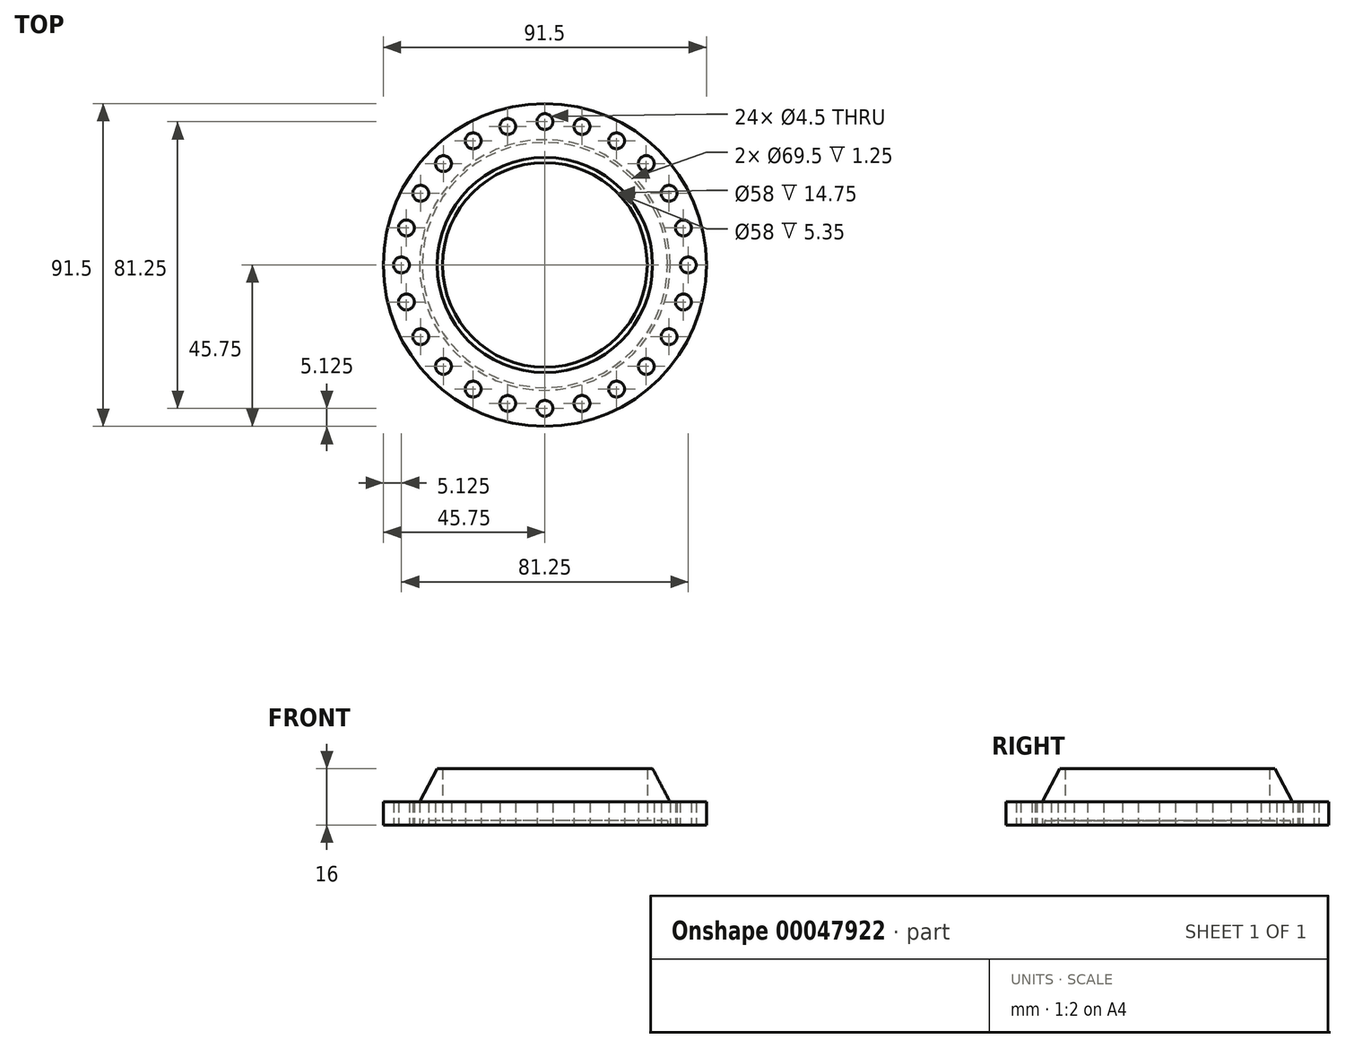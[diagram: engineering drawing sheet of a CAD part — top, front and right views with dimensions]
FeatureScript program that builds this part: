
annotation { "Feature Type Name" : "Feature", "Feature Type Description" : "" }
export const myFeature = defineFeature(function(context is Context, id is Id, definition is map)
    precondition{}
    {
        {
            var Q0;
            Q0=qCreatedBy(makeId("Top.planeOp"),FACE);
            var sketch = newSketch(context, id + "F0", { "sketchPlane" : qUnion([Q0])});
            skCircle(sketch, "E0", {"center": v(0, 0) * mm, "radius": 45.75 * mm});
            skCircle(sketch, "E1", {"center": v(0, 0) * mm, "radius": 40.62 * mm});
            skCircle(sketch, "E2", {"center": v(-40.62, 0) * mm, "radius": 2.25 * mm});
            skCircle(sketch, "E3", {"center": v(0, 0) * mm, "radius": 29 * mm});
            skCircle(sketch, "E4", {"center": v(0, 0) * mm, "radius": 35.5 * mm});
            skCircle(sketch, "E5.1.0", {"center": v(-39.24, -10.51) * mm, "radius": 2.25 * mm});
            skCircle(sketch, "E5.2.0", {"center": v(-35.18, -20.31) * mm, "radius": 2.25 * mm});
            skCircle(sketch, "E6.1.3.0", {"center": v(-28.73, -28.73) * mm, "radius": 2.25 * mm});
            skCircle(sketch, "E6.1.4.0", {"center": v(-20.31, -35.18) * mm, "radius": 2.25 * mm});
            skCircle(sketch, "E6.1.5.0", {"center": v(-10.51, -39.24) * mm, "radius": 2.25 * mm});
            skCircle(sketch, "E6.1.6.0", {"center": v(0, -40.62) * mm, "radius": 2.25 * mm});
            skCircle(sketch, "E6.1.7.0", {"center": v(10.51, -39.24) * mm, "radius": 2.25 * mm});
            skCircle(sketch, "E6.1.8.0", {"center": v(20.31, -35.18) * mm, "radius": 2.25 * mm});
            skCircle(sketch, "E6.1.9.0", {"center": v(28.73, -28.73) * mm, "radius": 2.25 * mm});
            skCircle(sketch, "E6.1.10.0", {"center": v(35.18, -20.31) * mm, "radius": 2.25 * mm});
            skCircle(sketch, "E6.1.11.0", {"center": v(39.24, -10.51) * mm, "radius": 2.25 * mm});
            skCircle(sketch, "E6.1.12.0", {"center": v(40.62, 0) * mm, "radius": 2.25 * mm});
            skCircle(sketch, "E6.1.13.0", {"center": v(39.24, 10.51) * mm, "radius": 2.25 * mm});
            skCircle(sketch, "E6.1.14.0", {"center": v(35.18, 20.31) * mm, "radius": 2.25 * mm});
            skCircle(sketch, "E6.1.15.0", {"center": v(28.73, 28.73) * mm, "radius": 2.25 * mm});
            skCircle(sketch, "E6.1.16.0", {"center": v(20.31, 35.18) * mm, "radius": 2.25 * mm});
            skCircle(sketch, "E6.1.17.0", {"center": v(10.51, 39.24) * mm, "radius": 2.25 * mm});
            skCircle(sketch, "E6.1.18.0", {"center": v(0, 40.62) * mm, "radius": 2.25 * mm});
            skCircle(sketch, "E6.1.19.0", {"center": v(-10.51, 39.24) * mm, "radius": 2.25 * mm});
            skCircle(sketch, "E6.1.20.0", {"center": v(-20.31, 35.18) * mm, "radius": 2.25 * mm});
            skCircle(sketch, "E6.1.21.0", {"center": v(-28.73, 28.73) * mm, "radius": 2.25 * mm});
            skCircle(sketch, "E6.1.22.0", {"center": v(-35.18, 20.31) * mm, "radius": 2.25 * mm});
            skCircle(sketch, "E7.1.23.0", {"center": v(-39.24, 10.51) * mm, "radius": 2.25 * mm});
            skSolve(sketch);
        }
        {
            var Q0;
            Q0=makeQuery(id+"F0.imprint","IMPRINT",FACE,{"disambiguationData":[TD([[makeQuery(id+"F0.imprint","IMPRINT",EDGE,{"derivedFrom":sQuery(id+"F0.wireOp",EDGE,"E0")}),1.0]])]});
            var Q1;
            Q1=makeQuery(id+"F0.imprint","IMPRINT",FACE,{"disambiguationData":[TD([[makeQuery(id+"F0.imprint","IMPRINT",EDGE,{"derivedFrom":sQuery(id+"F0.wireOp",EDGE,"E4")}),-1.0]])]});
            var Q2;
            Q2=makeQuery(id+"F0.imprint","IMPRINT",FACE,{"disambiguationData":[TD([[makeQuery(id+"F0.imprint","IMPRINT",EDGE,{"derivedFrom":sQuery(id+"F0.wireOp",EDGE,"E3")}),-1.0]])]});
            var Q3;
            Q3=sQuery(id+"F0.wireOp",EDGE,"E0");
            var Q4;
            Q4=sQuery(id+"F0.wireOp",EDGE,"E7.1.23.0");
            var Q5;
            Q5=sQuery(id+"F0.wireOp",EDGE,"E2");
            var Q6;
            Q6=sQuery(id+"F0.wireOp",EDGE,"E5.2.0");
            var Q7;
            Q7=sQuery(id+"F0.wireOp",EDGE,"E6.1.22.0");
            var Q8;
            Q8=sQuery(id+"F0.wireOp",EDGE,"E6.1.21.0");
            var Q9;
            Q9=sQuery(id+"F0.wireOp",EDGE,"E6.1.20.0");
            var Q10;
            Q10=sQuery(id+"F0.wireOp",EDGE,"E6.1.19.0");
            var Q11;
            Q11=sQuery(id+"F0.wireOp",EDGE,"E6.1.18.0");
            var Q12;
            Q12=sQuery(id+"F0.wireOp",EDGE,"E6.1.17.0");
            var Q13;
            Q13=sQuery(id+"F0.wireOp",EDGE,"E6.1.16.0");
            var Q14;
            Q14=sQuery(id+"F0.wireOp",EDGE,"E6.1.15.0");
            var Q15;
            Q15=sQuery(id+"F0.wireOp",EDGE,"E6.1.14.0");
            var Q16;
            Q16=sQuery(id+"F0.wireOp",EDGE,"E6.1.13.0");
            var Q17;
            Q17=sQuery(id+"F0.wireOp",EDGE,"E6.1.12.0");
            var Q18;
            Q18=sQuery(id+"F0.wireOp",EDGE,"E6.1.11.0");
            var Q19;
            Q19=sQuery(id+"F0.wireOp",EDGE,"E6.1.10.0");
            var Q20;
            Q20=sQuery(id+"F0.wireOp",EDGE,"E6.1.9.0");
            var Q21;
            Q21=sQuery(id+"F0.wireOp",EDGE,"E6.1.8.0");
            var Q22;
            Q22=sQuery(id+"F0.wireOp",EDGE,"E6.1.7.0");
            var Q23;
            Q23=sQuery(id+"F0.wireOp",EDGE,"E6.1.6.0");
            var Q24;
            Q24=sQuery(id+"F0.wireOp",EDGE,"E6.1.5.0");
            var Q25;
            Q25=sQuery(id+"F0.wireOp",EDGE,"E6.1.4.0");
            var Q26;
            Q26=sQuery(id+"F0.wireOp",EDGE,"E6.1.3.0");
            var Q27;
            Q27=sQuery(id+"F0.wireOp",EDGE,"E5.1.0");
            var Q28;
            Q28=sQuery(id+"F0.wireOp",EDGE,"E4");
            var Q29;
            Q29=qCreatedBy(makeId("Front.planeOp"),FACE);
            extrude(context, id + "F1", {"entities" : qUnion([Q0, Q1, Q2]), "surfaceEntities" : qUnion([Q3, Q4, Q5, Q6, Q7, Q8, Q9, Q10, Q11, Q12, Q13, Q14, Q15, Q16, Q17, Q18, Q19, Q20, Q21, Q22, Q23, Q24, Q25, Q26, Q27, Q28]), "endBoundEntityFace" : qUnion([Q29]), "depth" : 6.6 * mm});
        }
        {
            var Q0;
            Q0=sQuery(id+"F0.wireOp",EDGE,"E3");
            extrude(context, id + "F2", {"bodyType" : ToolBodyType.SURFACE, "surfaceEntities" : qUnion([Q0]), "depth" : 16 * mm});
        }
        {
            var Q0;
            Q0=makeQuery(id+"F0.imprint","IMPRINT",FACE,{"disambiguationData":[TD([[makeQuery(id+"F0.imprint","IMPRINT",EDGE,{"derivedFrom":sQuery(id+"F0.wireOp",EDGE,"E3")}),-1.0]])]});
            extrude(context, id + "F3", {"entities" : qUnion([Q0]), "depth" : 16 * mm});
        }
        {
            var Q0;
            Q0=makeQuery(id+"F3.opExtrude","CAP_EDGE",EDGE,{"disambiguationData":[OSD([sQuery(id+"F0.wireOp",EDGE,"E4")])],"isStart":false});
            chamfer(context, id + "F4", {"entities" : qUnion([Q0]), "chamferType" : ChamferType.TWO_OFFSETS, "width1" : 5 * mm, "oppositeDirection" : false, "width2" : 9.5 * mm, "tangentPropagation" : true});
        }
        {
            var Q0;
            Q0=qCreatedBy(makeId("Top.planeOp"),FACE);
            var sketch = newSketch(context, id + "F5", { "sketchPlane" : qUnion([Q0])});
            skCircle(sketch, "E8", {"center": v(0, 0) * mm, "radius": 34.75 * mm});
            skSolve(sketch);
        }
        {
            var Q0;
            Q0=makeQuery(id+"F5.imprint","IMPRINT",FACE,{"disambiguationData":[TD([[makeQuery(id+"F5.imprint","IMPRINT",EDGE,{"derivedFrom":sQuery(id+"F5.wireOp",EDGE,"E8")}),1.0]])]});
            extrude(context, id + "F6", {"entities" : qUnion([Q0]), "operationType" : NewBodyOperationType.REMOVE, "depth" : 1.25 * mm});
        }
    });
